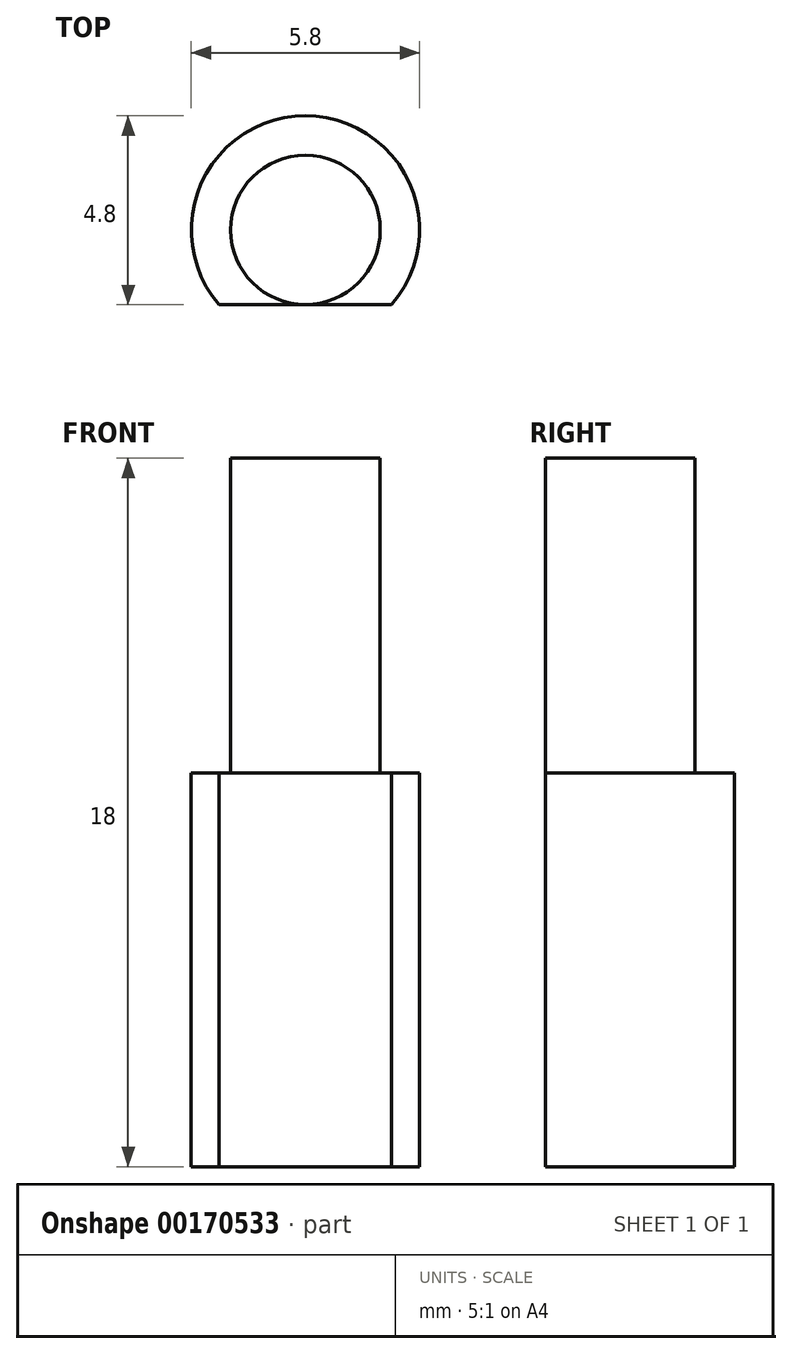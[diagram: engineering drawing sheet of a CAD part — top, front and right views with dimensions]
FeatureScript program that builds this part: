
annotation { "Feature Type Name" : "Feature", "Feature Type Description" : "" }
export const myFeature = defineFeature(function(context is Context, id is Id, definition is map)
    precondition{}
    {
        {
            var Q0;
            Q0=qCreatedBy(makeId("Top.planeOp"),FACE);
            var sketch = newSketch(context, id + "F0", { "sketchPlane" : qUnion([Q0])});
            skCircle(sketch, "E0", {"center": v(0, 0) * mm, "radius": 1.9 * mm});
            skSolve(sketch);
        }
        {
            var Q0;
            Q0 = qSketchRegion(id + "F0", true);
            extrude(context, id + "F1", {"entities" : qUnion([Q0]), "depth" : 8 * mm});
        }
        {
            var Q0;
            Q0=makeQuery(id+"F1.opExtrude","CAP_FACE",FACE,{"disambiguationData":[OSD([sQuery(id+"F0.wireOp",EDGE,"E0")])],"isStart":true});
            var sketch = newSketch(context, id + "F2", { "sketchPlane" : qUnion([Q0])});
            skCircle(sketch, "E1", {"center": v(0, 0) * mm, "radius": 2.9 * mm});
            skSolve(sketch);
        }
        {
            var Q0;
            Q0 = qSketchRegion(id + "F2", true);
            extrude(context, id + "F3", {"entities" : qUnion([Q0]), "operationType" : NewBodyOperationType.ADD, "depth" : 10 * mm});
        }
        {
            var Q0;
            Q0=qCreatedBy(makeId("Front.planeOp"),FACE);
            cPlane(context, id + "F4", {"entities" : qUnion([Q0]), "cplaneType" : CPlaneType.OFFSET, "offset" : 1.9 * mm, "width" : 150 * mm, "height" : 150 * mm});
        }
        {
            var Q0;
            Q0=qCreatedBy(id+"F4.planeOp",FACE);
            var sketch = newSketch(context, id + "F5", { "sketchPlane" : qUnion([Q0])});
            skLineSegment(sketch, "E2.bottom", {"start": v(-8.93, -16.2) * mm, "end": v(9.86, -16.2) * mm});
            skLineSegment(sketch, "E2.top", {"start": v(-8.93, 15.82) * mm, "end": v(9.86, 15.82) * mm});
            skLineSegment(sketch, "E2.left", {"start": v(-8.93, -16.2) * mm, "end": v(-8.93, 15.82) * mm});
            skLineSegment(sketch, "E2.right", {"start": v(9.86, -16.2) * mm, "end": v(9.86, 15.82) * mm});
            skSolve(sketch);
        }
        {
            var Q0;
            Q0=makeQuery(id+"F5.imprint","IMPRINT",FACE,{"disambiguationData":[TD([[makeQuery(id+"F5.imprint","IMPRINT",EDGE,{"derivedFrom":sQuery(id+"F5.wireOp",EDGE,"E2.bottom")}),1.0]])]});
            extrude(context, id + "F6", {"entities" : qUnion([Q0]), "operationType" : NewBodyOperationType.REMOVE, "depth" : 25 * mm});
        }
    });
